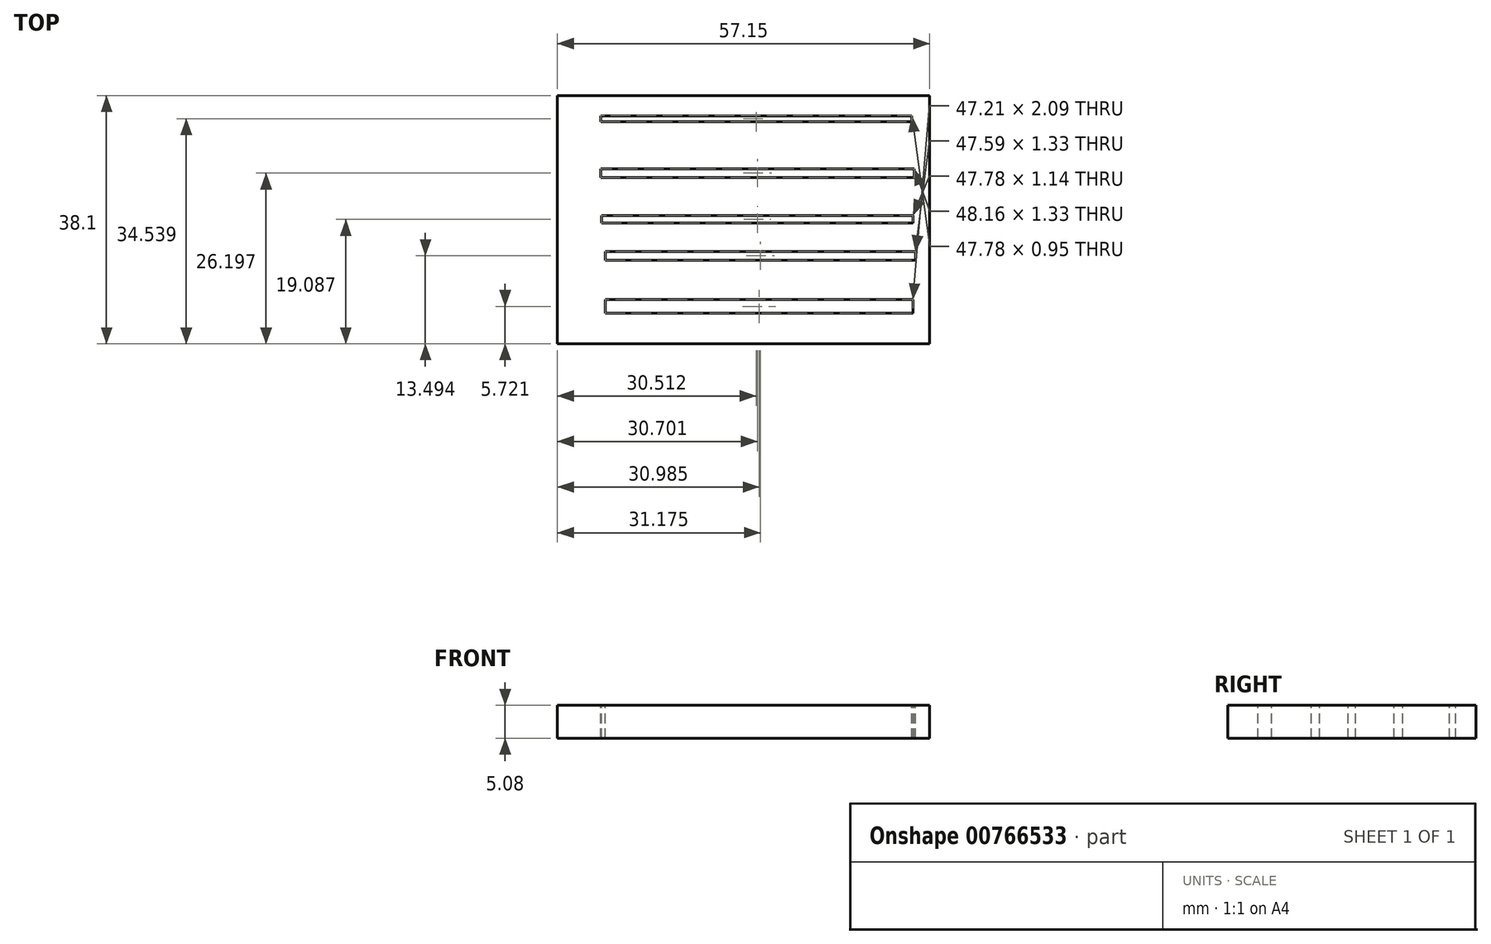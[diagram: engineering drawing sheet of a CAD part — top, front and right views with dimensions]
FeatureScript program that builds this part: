
annotation { "Feature Type Name" : "Feature", "Feature Type Description" : "" }
export const myFeature = defineFeature(function(context is Context, id is Id, definition is map)
    precondition{}
    {
        {
            var Q0;
            Q0=qCreatedBy(makeId("Top.planeOp"),FACE);
            var sketch = newSketch(context, id + "F0", { "sketchPlane" : qUnion([Q0])});
            skLineSegment(sketch, "E0.bottom", {"start": v(-57.15, 46.22) * mm, "end": v(0, 46.22) * mm});
            skLineSegment(sketch, "E0.top", {"start": v(-57.15, 8.12) * mm, "end": v(0, 8.12) * mm});
            skLineSegment(sketch, "E0.left", {"start": v(-57.15, 46.22) * mm, "end": v(-57.15, 8.12) * mm});
            skLineSegment(sketch, "E0.right", {"start": v(0, 46.22) * mm, "end": v(0, 8.12) * mm});
            skSolve(sketch);
        }
        {
            var Q0;
            Q0 = qSketchRegion(id + "F0", true);
            extrude(context, id + "F1", {"entities" : qUnion([Q0]), "depth" : 5.08 * mm, "offsetDistance" : 25.4 * mm});
        }
        {
            var Q0;
            Q0=makeQuery(id+"F1.opExtrude","CAP_FACE",FACE,{"disambiguationData":[OSD([sQuery(id+"F0.wireOp",EDGE,"E0.bottom"),sQuery(id+"F0.wireOp",EDGE,"E0.top"),sQuery(id+"F0.wireOp",EDGE,"E0.left"),sQuery(id+"F0.wireOp",EDGE,"E0.right")])],"isStart":false});
            var sketch = newSketch(context, id + "F2", { "sketchPlane" : qUnion([Q0])});
            skLineSegment(sketch, "E1.bottom", {"start": v(-50.53, 43.13) * mm, "end": v(-2.75, 43.13) * mm});
            skLineSegment(sketch, "E1.top", {"start": v(-50.53, 42.19) * mm, "end": v(-2.75, 42.19) * mm});
            skLineSegment(sketch, "E1.left", {"start": v(-50.53, 43.13) * mm, "end": v(-50.53, 42.19) * mm});
            skLineSegment(sketch, "E1.right", {"start": v(-2.75, 43.13) * mm, "end": v(-2.75, 42.19) * mm});
            skLineSegment(sketch, "E2.bottom", {"start": v(-50.53, 34.98) * mm, "end": v(-2.37, 34.98) * mm});
            skLineSegment(sketch, "E2.top", {"start": v(-50.53, 33.65) * mm, "end": v(-2.37, 33.65) * mm});
            skLineSegment(sketch, "E2.left", {"start": v(-50.53, 34.98) * mm, "end": v(-50.53, 33.65) * mm});
            skLineSegment(sketch, "E2.right", {"start": v(-2.37, 34.98) * mm, "end": v(-2.37, 33.65) * mm});
            skLineSegment(sketch, "E3.bottom", {"start": v(-50.34, 27.78) * mm, "end": v(-2.56, 27.78) * mm});
            skLineSegment(sketch, "E3.top", {"start": v(-50.34, 26.64) * mm, "end": v(-2.56, 26.64) * mm});
            skLineSegment(sketch, "E3.left", {"start": v(-50.34, 27.78) * mm, "end": v(-50.34, 26.64) * mm});
            skLineSegment(sketch, "E3.right", {"start": v(-2.56, 27.78) * mm, "end": v(-2.56, 26.64) * mm});
            skLineSegment(sketch, "E4.bottom", {"start": v(-49.77, 20.95) * mm, "end": v(-2.18, 20.95) * mm});
            skLineSegment(sketch, "E4.top", {"start": v(-49.77, 22.28) * mm, "end": v(-2.18, 22.28) * mm});
            skLineSegment(sketch, "E4.left", {"start": v(-49.77, 20.95) * mm, "end": v(-49.77, 22.28) * mm});
            skLineSegment(sketch, "E4.right", {"start": v(-2.18, 20.95) * mm, "end": v(-2.18, 22.28) * mm});
            skLineSegment(sketch, "E5.bottom", {"start": v(-49.77, 14.88) * mm, "end": v(-2.56, 14.88) * mm});
            skLineSegment(sketch, "E5.top", {"start": v(-49.77, 12.8) * mm, "end": v(-2.56, 12.8) * mm});
            skLineSegment(sketch, "E5.left", {"start": v(-49.77, 14.88) * mm, "end": v(-49.77, 12.8) * mm});
            skLineSegment(sketch, "E5.right", {"start": v(-2.56, 14.88) * mm, "end": v(-2.56, 12.8) * mm});
            skSolve(sketch);
        }
        {
            var Q0;
            Q0 = qSketchRegion(id + "F2", true);
            extrude(context, id + "F3", {"entities" : qUnion([Q0]), "operationType" : NewBodyOperationType.REMOVE, "oppositeDirection" : true, "depth" : 115163.6 * mm, "offsetDistance" : 25.4 * mm});
        }
    });
